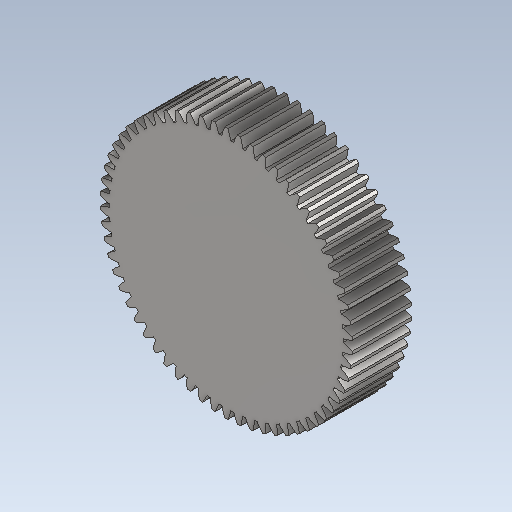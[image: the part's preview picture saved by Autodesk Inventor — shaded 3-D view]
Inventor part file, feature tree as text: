
AUTODESK INVENTOR PART (.ipt)
format: ipt  version: 2020.5 (Build 245400000, 400)  size: 423,424 bytes
history: native  units: mm (DEFAULTED — no unit token found)
features: plane x3, other x3, sketch x2, extrude x1
ambient origin geometry x8: Origin, YZ Plane, XZ Plane, XY Plane, X Axis, Y Axis, Z Axis, Center Point
bodies: Solid1 (feature_tree)
feature tree (9):
  extrude  "Extrusion1"  Depth=30.0mm TaperAngle=0.0deg
  plane  "Work Plane2"
  plane  "Work Plane8"
  plane  "Work Plane9"
  other  "Engranaje recto"
  sketch  "Sketch1"  dims[d0=127.2mm d1=30.0mm d2=0.0mm]
  sketch  "Sketch2"  dims[d3=124.0mm d4=10.0mm d5=0.0mm d16=82.0mm d17=0.0mm d34=0.506708mm d39=0.0mm d41=0.0mm d43=82.0mm d46=82.0mm d47=0.0mm d48=0.0mm]
  other  "Srf1"
  other  "Diámetro de separación"
